# Revit family: revitupgrade
name_source: partatom
category: Furniture
units: mm (PartAtom-declared; Revit-internal decimal feet)

## family parameters
Always vertical = Yes
Cut with Voids When Loaded = No
Enable Cutting in Views = No
OmniClass Number = 23.40.70.14.64.11
OmniClass Title = Office Furniture
Render Appearance Source = Family Geometry
Room Calculation Point = No
Shared = No
Work Plane-Based = No

## types (27) — shared parameters
Assembly Code = E2020200
Default Elevation = 0.00 mm
Description = Migration SE Pro is the next generation of height-adjustable desking with improved performance, robust stability and a design that is visually lighter and easily customizable.
Manufacturer = Steelcase
Release Date = November 2023
URL = https://www.steelcase.com

## per-type parameters (varying)
| type | Basic Height | Depth | Desk Height, MAX | Desk Height, MIN | Extended Height | Fixed Height | Style Number(s) | Width |
| Fixed Height - 700D x 1200W | No | 700.00 mm | 720.00 mm | 720.00 mm | No | Yes | MGDFLVQB, MGDEWSVQ | 1200.00 mm |
| Fixed Height - 750D x 1200W | No | 750.00 mm | 720.00 mm | 720.00 mm | No | Yes | MGDFLVQB, MGDEWSVQ | 1200.00 mm |
| Fixed Height - 700D x 1600W | No | 700.00 mm | 720.00 mm | 720.00 mm | No | Yes | MGDFLVQB, MGDEWSVQ | 1600.00 mm |
| Fixed Height - 700D x 1400W | No | 700.00 mm | 720.00 mm | 720.00 mm | No | Yes | MGDFLVQB, MGDEWSVQ | 1400.00 mm |
| Basic Height - 700D x 1600W | Yes | 700.00 mm | 1180.00 mm | 720.00 mm | No | No | MGDBLVQB, MGDEWSVQ | 1600.00 mm |
| Basic Height - 700D x 1400W | Yes | 700.00 mm | 1180.00 mm | 720.00 mm | No | No | MGDBLVQB, MGDEWSVQ | 1400.00 mm |
| Basic Height - 700D x 1200W | Yes | 700.00 mm | 1180.00 mm | 720.00 mm | No | No | MGDBLVQB, MGDEWSVQ | 1200.00 mm |
| Fixed Height - 800D x 1600W | No | 800.00 mm | 720.00 mm | 720.00 mm | No | Yes | MGDFLVQB, MGDEWSVQ | 1600.00 mm |
| Fixed Height - 800D x 1400W | No | 800.00 mm | 720.00 mm | 720.00 mm | No | Yes | MGDFLVQB, MGDEWSVQ | 1400.00 mm |
| Fixed Height - 800D x 1200W | No | 800.00 mm | 720.00 mm | 720.00 mm | No | Yes | MGDFLVQB, MGDEWSVQ | 1200.00 mm |
| Fixed Height - 750D x 1600W | No | 750.00 mm | 720.00 mm | 720.00 mm | No | Yes | MGDFLVQB, MGDEWSVQ | 1600.00 mm |
| Fixed Height - 750D x 1400W | No | 750.00 mm | 720.00 mm | 720.00 mm | No | Yes | MGDFLVQB, MGDEWSVQ | 1400.00 mm |
| Extended Height - 800D x 1600W | No | 800.00 mm | 1250.00 mm | 650.00 mm | Yes | No | MGDELVQB, MGDEWSVQ | 1600.00 mm |
| Extended Height - 800D x 1400W | No | 800.00 mm | 1250.00 mm | 650.00 mm | Yes | No | MGDELVQB, MGDEWSVQ | 1400.00 mm |
| Extended Height - 800D x 1200W | No | 800.00 mm | 1250.00 mm | 650.00 mm | Yes | No | MGDELVQB, MGDEWSVQ | 1200.00 mm |
| Extended Height - 750D x 1600W | No | 750.00 mm | 1250.00 mm | 650.00 mm | Yes | No | MGDELVQB, MGDEWSVQ | 1600.00 mm |
| Extended Height - 750D x 1400W | No | 750.00 mm | 1250.00 mm | 650.00 mm | Yes | No | MGDELVQB, MGDEWSVQ | 1400.00 mm |
| Extended Height - 750D x 1200W | No | 750.00 mm | 1250.00 mm | 650.00 mm | Yes | No | MGDELVQB, MGDEWSVQ | 1200.00 mm |
| Extended Height - 700D x 1600W | No | 700.00 mm | 1250.00 mm | 650.00 mm | Yes | No | MGDELVQB, MGDEWSVQ | 1600.00 mm |
| Extended Height - 700D x 1400W | No | 700.00 mm | 1250.00 mm | 650.00 mm | Yes | No | MGDELVQB, MGDEWSVQ | 1400.00 mm |
| Extended Height - 700D x 1200W | No | 700.00 mm | 1250.00 mm | 650.00 mm | Yes | No | MGDELVQB, MGDEWSVQ | 1200.00 mm |
| Basic Height - 800D x 1600W | Yes | 800.00 mm | 1180.00 mm | 720.00 mm | No | No | MGDBLVQB, MGDEWSVQ | 1600.00 mm |
| Basic Height - 800D x 1400W | Yes | 800.00 mm | 1180.00 mm | 720.00 mm | No | No | MGDBLVQB, MGDEWSVQ | 1400.00 mm |
| Basic Height - 800D x 1200W | Yes | 800.00 mm | 1180.00 mm | 720.00 mm | No | No | MGDBLVQB, MGDEWSVQ | 1200.00 mm |
| Basic Height - 750D x 1600W | Yes | 750.00 mm | 1180.00 mm | 720.00 mm | No | No | MGDBLVQB, MGDEWSVQ | 1600.00 mm |
| Basic Height - 750D x 1400W | Yes | 750.00 mm | 1180.00 mm | 720.00 mm | No | No | MGDBLVQB, MGDEWSVQ | 1400.00 mm |
| Basic Height - 750D x 1200W | Yes | 750.00 mm | 1180.00 mm | 720.00 mm | No | No | MGDBLVQB, MGDEWSVQ | 1200.00 mm |

## geometry (parser evidence)
native form markers: Sweep x13
no freeform markers — native parametric forms only
